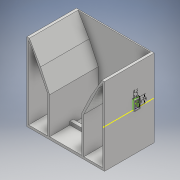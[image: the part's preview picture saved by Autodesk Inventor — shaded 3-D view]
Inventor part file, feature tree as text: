
AUTODESK INVENTOR PART (.ipt)
format: ipt  version: 2020.3 (Build 243373000, 373)  size: 220,672 bytes
history: native  units: mm
features: extrude x9, sketch x8, other x1, pattern_linear x1, projected_geometry x1
ambient origin geometry x8: Origin, YZ Plane, XZ Plane, XY Plane, X Axis, Y Axis, Z Axis, Center Point
bodies: Body1 (feature_tree)
feature tree (20):
  other  "Твердое тело1"
  extrude  "Выдавливание1"  Depth=230.0mm
  extrude  "Выдавливание2"  Depth=230.0mm
  extrude  "Выдавливание3"  Depth=66.0mm
  extrude  "Выдавливание4"  TaperAngle=120.0deg  [1 undecoded]
  extrude  "Выдавливание5"  Depth=20.071286mm
  extrude  "Выдавливание6"  Depth=66.0mm
  sketch  "Эскиз7"
  extrude  "Выдавливание7"  TaperAngle=60.0deg  [1 undecoded]
  extrude  "Выдавливание8"  Depth=11.34464mm
  pattern_linear  "Прямоуг.массив1"  Count1=15 Spacing1=0.0mm
  extrude  "Выдавливание9"  Depth=135161.0mm TaperAngle=0.0deg
  sketch  "Эскиз1"
  sketch  "Эскиз2"
  sketch  "Эскиз3"
  sketch  "Эскиз4"
  sketch  "Эскиз5"
  sketch  "Эскиз6"
  projected_geometry  "Спроецированная петля1"
  sketch  "Эскиз8"
note: 2 required parameter values undecoded (feature->parameter linkage not recoverable at this tier; creation-order binding heuristic only, values carry confidence <= 0.55)
